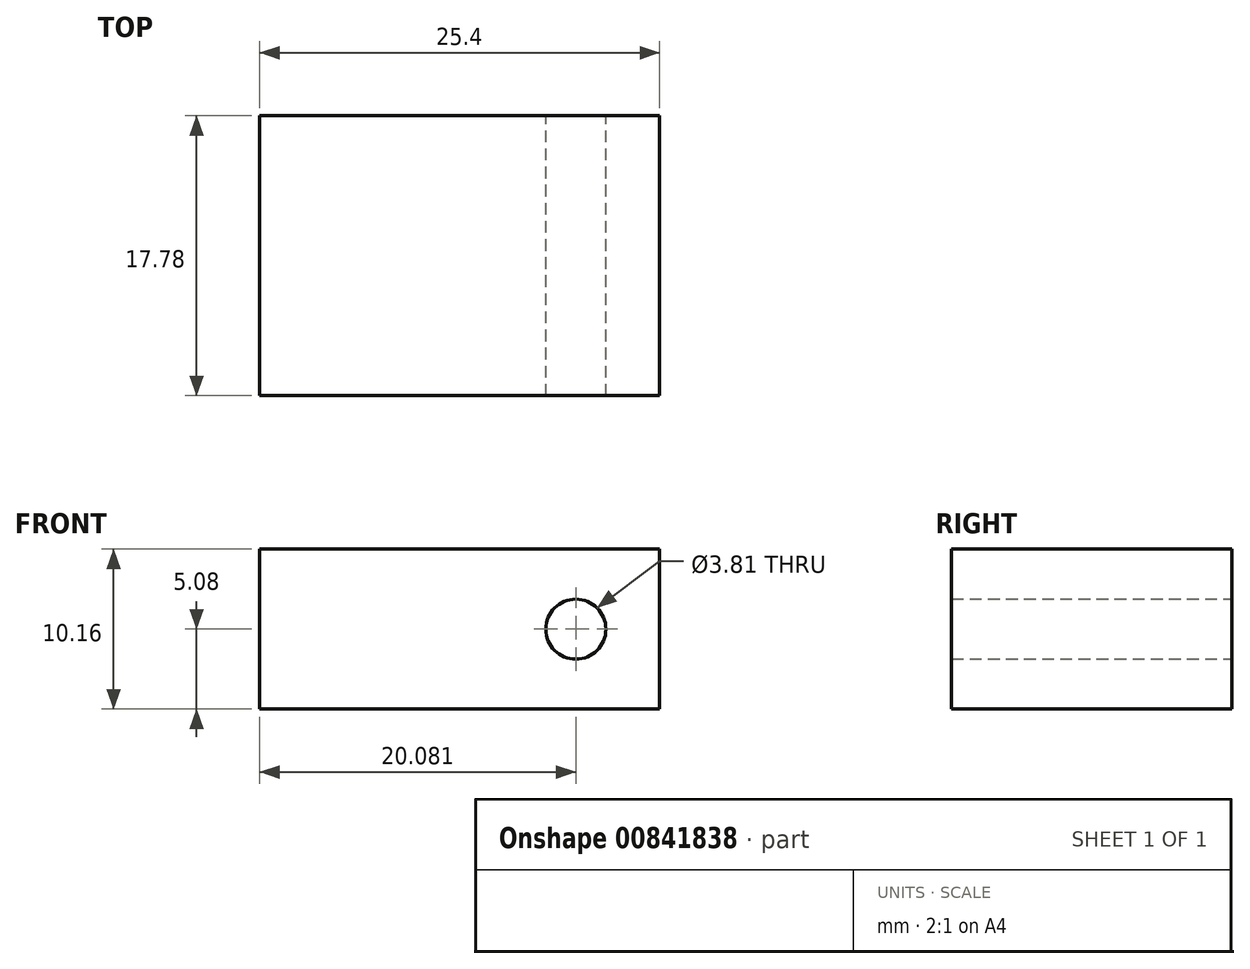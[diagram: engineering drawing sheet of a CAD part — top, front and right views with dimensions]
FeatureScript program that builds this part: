
annotation { "Feature Type Name" : "Feature", "Feature Type Description" : "" }
export const myFeature = defineFeature(function(context is Context, id is Id, definition is map)
    precondition{}
    {
        {
            var Q0;
            Q0=qCreatedBy(makeId("Front.planeOp"),FACE);
            var sketch = newSketch(context, id + "F0", { "sketchPlane" : qUnion([Q0])});
            skLineSegment(sketch, "E0.bottom", {"start": v(12.7, -5.08) * mm, "end": v(-12.7, -5.08) * mm});
            skLineSegment(sketch, "E0.top", {"start": v(12.7, 5.08) * mm, "end": v(-12.7, 5.08) * mm});
            skLineSegment(sketch, "E0.left", {"start": v(12.7, -5.08) * mm, "end": v(12.7, 5.08) * mm});
            skLineSegment(sketch, "E0.right", {"start": v(-12.7, -5.08) * mm, "end": v(-12.7, 5.08) * mm});
            skPoint(sketch, "E0.middle", {"position": v(0, 0) * mm});
            skCircle(sketch, "E1", {"center": v(7.38, 0) * mm, "radius": 1.9 * mm});
            skSolve(sketch);
        }
        {
            var Q0;
            Q0=makeQuery(id+"F0.imprint","IMPRINT",FACE,{"disambiguationData":[TD([[makeQuery(id+"F0.imprint","IMPRINT",EDGE,{"derivedFrom":sQuery(id+"F0.wireOp",EDGE,"E0.bottom")}),-1.0]])]});
            extrude(context, id + "F1", {"entities" : qUnion([Q0]), "depth" : 17.78 * mm, "offsetDistance" : 25.4 * mm});
        }
    });
